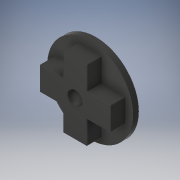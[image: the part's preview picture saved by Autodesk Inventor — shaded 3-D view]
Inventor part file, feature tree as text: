
AUTODESK INVENTOR PART (.ipt)
format: ipt  version: 2019 (Build 230136000, 136)  size: 212,480 bytes
history: native  units: mm
features: extrude x5, sketch x5, fillet x3
ambient origin geometry x8: Origin, YZ Plane, XZ Plane, XY Plane, X Axis, Y Axis, Z Axis, Center Point
bodies: Solide1 (feature_tree)
feature tree (13):
  extrude  "Extrusion1"  Depth=25.5mm
  extrude  "Extrusion2"  Depth=1.7mm TaperAngle=0.0deg
  extrude  "Extrusion3"  Depth=7.0mm
  extrude  "Extrusion4"  Depth=7.0mm
  fillet  "Congé1"  Radius=3.5mm
  extrude  "Extrusion5"  Depth=3.5mm
  fillet  "Congé2"  Radius=21.0mm
  fillet  "Congé3"  Radius=21.0mm
  sketch  "Esquisse1"
  sketch  "Esquisse2"
  sketch  "Esquisse3"
  sketch  "Esquisse4"
  sketch  "Esquisse5"
